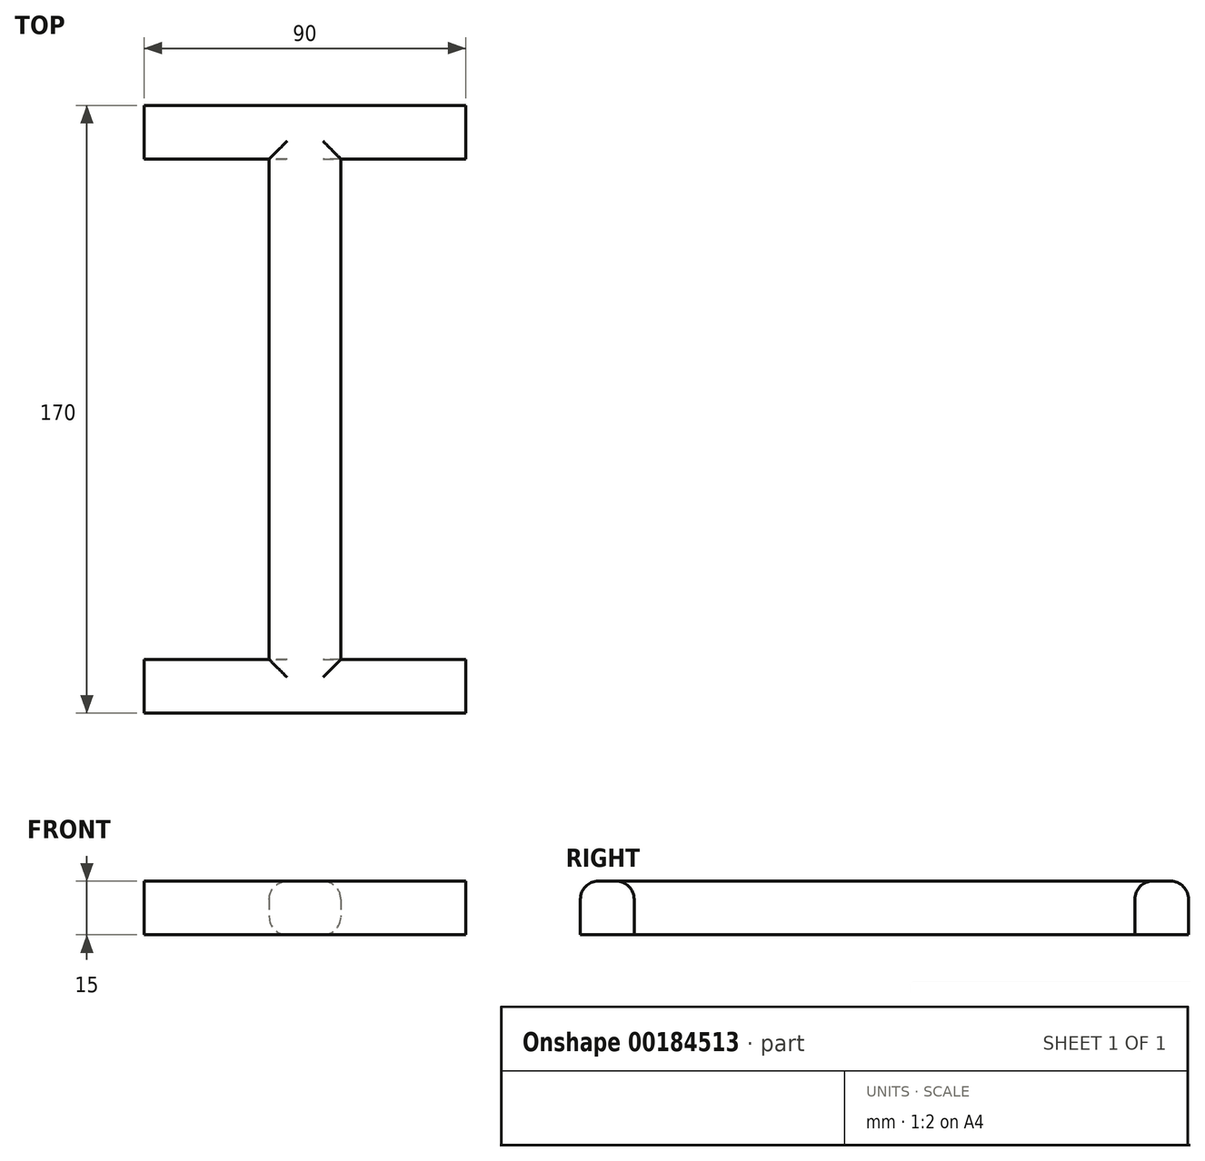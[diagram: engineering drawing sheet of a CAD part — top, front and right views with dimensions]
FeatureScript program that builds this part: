
annotation { "Feature Type Name" : "Feature", "Feature Type Description" : "" }
export const myFeature = defineFeature(function(context is Context, id is Id, definition is map)
    precondition{}
    {
        {
            var Q0;
            Q0=qCreatedBy(makeId("Top.planeOp"),FACE);
            var sketch = newSketch(context, id + "F0", { "sketchPlane" : qUnion([Q0])});
            skLineSegment(sketch, "E0.left", {"start": v(0, 0) * mm, "end": v(0, -140) * mm});
            skLineSegment(sketch, "E0.right", {"start": v(20, 0) * mm, "end": v(20, -140) * mm});
            skLineSegment(sketch, "E1.bottom", {"start": v(-35, 15) * mm, "end": v(55, 15) * mm});
            skLineSegment(sketch, "E1.top", {"start": v(-35, 0) * mm, "end": v(0, 0) * mm});
            skLineSegment(sketch, "E1.left", {"start": v(-35, 15) * mm, "end": v(-35, 0) * mm});
            skLineSegment(sketch, "E1.right", {"start": v(55, 15) * mm, "end": v(55, 0) * mm});
            skLineSegment(sketch, "E2.bottom", {"start": v(-35, -140) * mm, "end": v(0, -140) * mm});
            skLineSegment(sketch, "E2.top", {"start": v(-35, -155) * mm, "end": v(55, -155) * mm});
            skLineSegment(sketch, "E2.left", {"start": v(-35, -140) * mm, "end": v(-35, -155) * mm});
            skLineSegment(sketch, "E2.right", {"start": v(55, -140) * mm, "end": v(55, -155) * mm});
            skLineSegment(sketch, "E3.trimOffspring", {"start": v(20, 0) * mm, "end": v(55, 0) * mm});
            skLineSegment(sketch, "E4.trimOffspring", {"start": v(20, -140) * mm, "end": v(55, -140) * mm});
            skSolve(sketch);
        }
        {
            var Q0;
            Q0 = qSketchRegion(id + "F0", true);
            extrude(context, id + "F1", {"entities" : qUnion([Q0]), "depth" : 15 * mm});
        }
        {
            var Q0;
            Q0=makeQuery(id+"F1.opExtrude","CAP_EDGE",EDGE,{"disambiguationData":[OSD([sQuery(id+"F0.wireOp",EDGE,"E1.bottom")])],"isStart":false});
            var Q1;
            Q1=makeQuery(id+"F1.opExtrude","CAP_EDGE",EDGE,{"disambiguationData":[OSD([sQuery(id+"F0.wireOp",EDGE,"E2.top")])],"isStart":false});
            var Q2;
            Q2=makeQuery(id+"F1.opExtrude","CAP_EDGE",EDGE,{"disambiguationData":[OSD([sQuery(id+"F0.wireOp",EDGE,"E0.left")])],"isStart":false});
            var Q3;
            Q3=makeQuery(id+"F1.opExtrude","CAP_EDGE",EDGE,{"disambiguationData":[OSD([sQuery(id+"F0.wireOp",EDGE,"E0.right")])],"isStart":false});
            var Q4;
            Q4=makeQuery(id+"F1.opExtrude","CAP_EDGE",EDGE,{"disambiguationData":[OSD([sQuery(id+"F0.wireOp",EDGE,"E0.left")])],"isStart":true});
            var Q5;
            Q5=makeQuery(id+"F1.opExtrude","CAP_EDGE",EDGE,{"disambiguationData":[OSD([sQuery(id+"F0.wireOp",EDGE,"E0.right")])],"isStart":true});
            var Q6;
            Q6=makeQuery(id+"F1.opExtrude","CAP_EDGE",EDGE,{"disambiguationData":[OSD([sQuery(id+"F0.wireOp",EDGE,"E1.top")])],"isStart":false});
            var Q7;
            Q7=makeQuery(id+"F1.opExtrude","CAP_EDGE",EDGE,{"disambiguationData":[OSD([sQuery(id+"F0.wireOp",EDGE,"E3.trimOffspring")])],"isStart":false});
            var Q8;
            Q8=makeQuery(id+"F1.opExtrude","CAP_EDGE",EDGE,{"disambiguationData":[OSD([sQuery(id+"F0.wireOp",EDGE,"E2.bottom")])],"isStart":false});
            var Q9;
            Q9=makeQuery(id+"F1.opExtrude","CAP_EDGE",EDGE,{"disambiguationData":[OSD([sQuery(id+"F0.wireOp",EDGE,"E4.trimOffspring")])],"isStart":false});
            fillet(context, id + "F2", {"entities" : qUnion([Q0, Q1, Q2, Q3, Q4, Q5, Q6, Q7, Q8, Q9]), "radius" : 5 * mm, "tangentPropagation" : true, "allowEdgeOverflow" : false});
        }
    });
